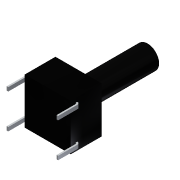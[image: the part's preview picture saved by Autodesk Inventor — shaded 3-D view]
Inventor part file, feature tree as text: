
AUTODESK INVENTOR PART (.ipt)
format: ipt  version: 2015 SP1 (Build 190203100, 203)  size: 145,408 bytes
history: native  units: mm
features: sketch x7, projected_geometry x3, other x2, sweep x2, extrude x1, loft x1
ambient origin geometry x8: Origin, YZ Plane, XZ Plane, XY Plane, X Axis, Y Axis, Z Axis, Center Point
bodies: Body1 (feature_tree)
feature tree (16):
  other  "Твердое тело1"
  extrude  "Выдавливание1"  Depth=6.0mm
  sketch  "Эскиз2"
  other  "РабПлоскость1"
  loft  "Лофт1"
  sketch  "Эскиз4"
  sketch  "Эскиз5"
  sketch  "Эскиз6"
  sweep  "Сдвиг1"
  sweep  "Сдвиг2"
  sketch  "Эскиз7"
  sketch  "Эскиз1"
  sketch  "Эскиз3"
  projected_geometry  "Спроецированная петля1"
  projected_geometry  "Спроецированная петля2"
  projected_geometry  "Спроецированная петля3"
